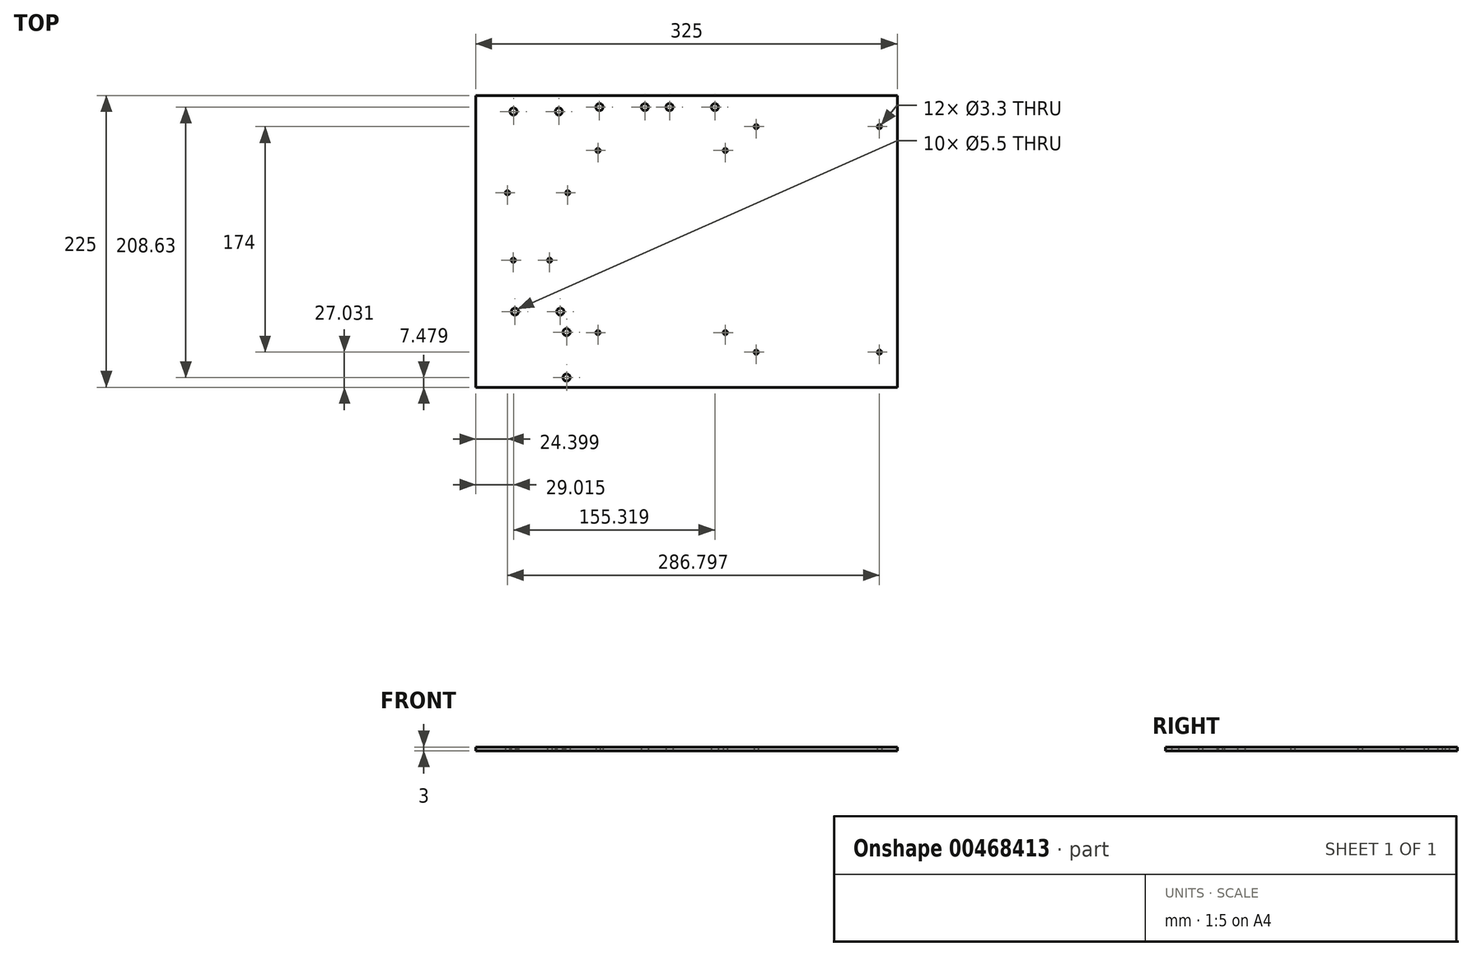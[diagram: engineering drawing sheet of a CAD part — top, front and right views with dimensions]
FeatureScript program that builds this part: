
annotation { "Feature Type Name" : "Feature", "Feature Type Description" : "" }
export const myFeature = defineFeature(function(context is Context, id is Id, definition is map)
    precondition{}
    {
        {
            var Q0;
            Q0=qCreatedBy(makeId("Top.planeOp"),FACE);
            var sketch = newSketch(context, id + "F0", { "sketchPlane" : qUnion([Q0])});
            skLineSegment(sketch, "E0.bottom", {"start": v(162.5, 112.5) * mm, "end": v(-162.5, 112.5) * mm});
            skLineSegment(sketch, "E0.top", {"start": v(162.5, -112.5) * mm, "end": v(-162.5, -112.5) * mm});
            skLineSegment(sketch, "E0.left", {"start": v(162.5, 112.5) * mm, "end": v(162.5, -112.5) * mm});
            skLineSegment(sketch, "E0.right", {"start": v(-162.5, 112.5) * mm, "end": v(-162.5, -112.5) * mm});
            skPoint(sketch, "E0.middle", {"position": v(0, 0) * mm});
            skLineSegment(sketch, "E1.bottom", {"start": v(157.5, 106.22) * mm, "end": v(44.5, 106.22) * mm, "construction": true});
            skLineSegment(sketch, "E1.top", {"start": v(157.5, -107.78) * mm, "end": v(44.5, -107.78) * mm, "construction": true});
            skLineSegment(sketch, "E1.left", {"start": v(157.5, 106.22) * mm, "end": v(157.5, -107.78) * mm, "construction": true});
            skLineSegment(sketch, "E1.right", {"start": v(44.5, 106.22) * mm, "end": v(44.5, -107.78) * mm, "construction": true});
            skLineSegment(sketch, "E2.bottom", {"start": v(34.17, 86.46) * mm, "end": v(-74.83, 86.46) * mm, "construction": true});
            skLineSegment(sketch, "E2.top", {"start": v(34.17, -88.54) * mm, "end": v(-74.83, -88.54) * mm, "construction": true});
            skLineSegment(sketch, "E2.left", {"start": v(34.17, 86.46) * mm, "end": v(34.17, -88.54) * mm, "construction": true});
            skLineSegment(sketch, "E2.right", {"start": v(-74.83, 86.46) * mm, "end": v(-74.83, -88.54) * mm, "construction": true});
            skLineSegment(sketch, "E3.bottom", {"start": v(-143.1, 65.38) * mm, "end": v(-88.1, 65.38) * mm, "construction": true});
            skLineSegment(sketch, "E3.top", {"start": v(-143.1, -24.62) * mm, "end": v(-88.1, -24.62) * mm, "construction": true});
            skLineSegment(sketch, "E3.left", {"start": v(-143.1, 65.38) * mm, "end": v(-143.1, -24.62) * mm, "construction": true});
            skLineSegment(sketch, "E3.right", {"start": v(-88.1, 65.38) * mm, "end": v(-88.1, -24.62) * mm, "construction": true});
            skLineSegment(sketch, "E4.bottom", {"start": v(-68.31, 70.13) * mm, "end": v(29.89, 70.13) * mm, "construction": true});
            skLineSegment(sketch, "E4.top", {"start": v(-68.31, -70.37) * mm, "end": v(29.89, -70.37) * mm, "construction": true});
            skLineSegment(sketch, "E4.left", {"start": v(-68.31, 70.13) * mm, "end": v(-68.31, -70.37) * mm, "construction": true});
            skLineSegment(sketch, "E4.right", {"start": v(29.89, 70.13) * mm, "end": v(29.89, -70.37) * mm, "construction": true});
            skLineSegment(sketch, "E5.bottom", {"start": v(53.7, 88.53) * mm, "end": v(148.7, 88.53) * mm, "construction": true});
            skLineSegment(sketch, "E5.top", {"start": v(53.7, -85.47) * mm, "end": v(148.7, -85.47) * mm, "construction": true});
            skLineSegment(sketch, "E5.left", {"start": v(53.7, 88.53) * mm, "end": v(53.7, -85.47) * mm, "construction": true});
            skLineSegment(sketch, "E5.right", {"start": v(148.7, 88.53) * mm, "end": v(148.7, -85.47) * mm, "construction": true});
            skLineSegment(sketch, "E6", {"start": v(-133.6, -14.52) * mm, "end": v(-105.6, -14.52) * mm, "construction": true});
            skLineSegment(sketch, "E7", {"start": v(-105.6, -14.52) * mm, "end": v(-105.6, 37.48) * mm, "construction": true});
            skLineSegment(sketch, "E8", {"start": v(-133.6, -14.52) * mm, "end": v(-133.6, 37.48) * mm, "construction": true});
            skLineSegment(sketch, "E9", {"start": v(-133.6, 37.48) * mm, "end": v(-138.1, 37.48) * mm, "construction": true});
            skLineSegment(sketch, "E10", {"start": v(-105.6, 37.48) * mm, "end": v(-91.6, 37.48) * mm, "construction": true});
            skLineSegment(sketch, "E11", {"start": v(-133.48, 100.2) * mm, "end": v(-98.48, 100.2) * mm, "construction": true});
            skLineSegment(sketch, "E12", {"start": v(-132.36, -54.18) * mm, "end": v(-97.36, -54.18) * mm, "construction": true});
            skLineSegment(sketch, "E13", {"start": v(-67.16, 103.6) * mm, "end": v(-32.16, 103.6) * mm, "construction": true});
            skLineSegment(sketch, "E14", {"start": v(-13.17, 103.6) * mm, "end": v(21.83, 103.6) * mm, "construction": true});
            skLineSegment(sketch, "E15", {"start": v(-92.5, -70.02) * mm, "end": v(-92.5, -105.02) * mm, "construction": true});
            skSolve(sketch);
        }
        {
            var Q0;
            Q0 = qSketchRegion(id + "F0", true);
            extrude(context, id + "F1", {"entities" : qUnion([Q0]), "depth" : 3 * mm});
        }
        {
            var Q0;
            Q0=sQuery(id+"F0.wireOp",VERTEX,"E5.bottom.end");
            var Q1;
            Q1=sQuery(id+"F0.wireOp",VERTEX,"E5.bottom.start");
            var Q2;
            Q2=sQuery(id+"F0.wireOp",VERTEX,"E5.top.end");
            var Q3;
            Q3=sQuery(id+"F0.wireOp",VERTEX,"E5.left.end");
            var Q4;
            Q4=sQuery(id+"F0.wireOp",VERTEX,"E4.bottom.start");
            var Q5;
            Q5=sQuery(id+"F0.wireOp",VERTEX,"E4.right.start");
            var Q6;
            Q6=sQuery(id+"F0.wireOp",VERTEX,"E4.right.end");
            var Q7;
            Q7=sQuery(id+"F0.wireOp",VERTEX,"E4.top.start");
            var Q8;
            Q8=sQuery(id+"F0.wireOp",VERTEX,"E10.end");
            var Q9;
            Q9=sQuery(id+"F0.wireOp",VERTEX,"E7.start");
            var Q10;
            Q10=sQuery(id+"F0.wireOp",VERTEX,"E6.start");
            var Q11;
            Q11=sQuery(id+"F0.wireOp",VERTEX,"E9.end");
            var Q12;
            Q12=makeQuery(id+"F1.opExtrude","SWEPT_BODY",BODY,{"disambiguationData":[OSD([sQuery(id+"F0.wireOp",EDGE,"E0.bottom"),sQuery(id+"F0.wireOp",EDGE,"E0.top"),sQuery(id+"F0.wireOp",EDGE,"E0.left"),sQuery(id+"F0.wireOp",EDGE,"E0.right")])]});
            hole(context, id + "F2", {"style" : HoleStyle.SIMPLE, "endStyle" : HoleEndStyle.BLIND, "oppositeDirection" : true, "standardTappedOrClearance" : lookupTablePath({ "standard" : "ISO", "fit" : "Normal", "size" : "M3", "type" : "Clearance" }), "standardBlindInLast" : lookupTablePath({ "fit" : "Standard", "standard" : "ISO", "size" : "M3", "type" : "Clearance" }), "holeDiameter" : 3.3 * mm, "holeDepth" : 15 * mm, "isTappedThrough" : true, "tappedDepth" : 12 * mm, "tapClearance" : 3, "startFromSketch" : true, "locations" : qUnion([Q0, Q1, Q2, Q3, Q4, Q5, Q6, Q7, Q8, Q9, Q10, Q11]), "scope" : qUnion([Q12])});
        }
        {
            var Q0;
            Q0=sQuery(id+"F0.wireOp",VERTEX,"E11.start");
            var Q1;
            Q1=sQuery(id+"F0.wireOp",VERTEX,"E11.end");
            var Q2;
            Q2=sQuery(id+"F0.wireOp",VERTEX,"E13.start");
            var Q3;
            Q3=sQuery(id+"F0.wireOp",VERTEX,"E13.end");
            var Q4;
            Q4=sQuery(id+"F0.wireOp",VERTEX,"E14.start");
            var Q5;
            Q5=sQuery(id+"F0.wireOp",VERTEX,"E14.end");
            var Q6;
            Q6=sQuery(id+"F0.wireOp",VERTEX,"E15.start");
            var Q7;
            Q7=sQuery(id+"F0.wireOp",VERTEX,"E15.end");
            var Q8;
            Q8=sQuery(id+"F0.wireOp",VERTEX,"E12.end");
            var Q9;
            Q9=sQuery(id+"F0.wireOp",VERTEX,"E12.start");
            var Q10;
            Q10=makeQuery(id+"F1.opExtrude","SWEPT_BODY",BODY,{"disambiguationData":[OSD([sQuery(id+"F0.wireOp",EDGE,"E0.bottom"),sQuery(id+"F0.wireOp",EDGE,"E0.top"),sQuery(id+"F0.wireOp",EDGE,"E0.left"),sQuery(id+"F0.wireOp",EDGE,"E0.right")])]});
            hole(context, id + "F3", {"style" : HoleStyle.SIMPLE, "endStyle" : HoleEndStyle.BLIND, "oppositeDirection" : true, "standardTappedOrClearance" : lookupTablePath({ "standard" : "ISO", "fit" : "Normal", "size" : "M5", "type" : "Clearance" }), "standardBlindInLast" : lookupTablePath({ "fit" : "Standard", "standard" : "ISO", "size" : "M5", "type" : "Clearance" }), "holeDiameter" : 5.5 * mm, "holeDepth" : 15 * mm, "isTappedThrough" : true, "tappedDepth" : 12 * mm, "tapClearance" : 3, "startFromSketch" : true, "locations" : qUnion([Q0, Q1, Q2, Q3, Q4, Q5, Q6, Q7, Q8, Q9]), "scope" : qUnion([Q10])});
        }
    });
